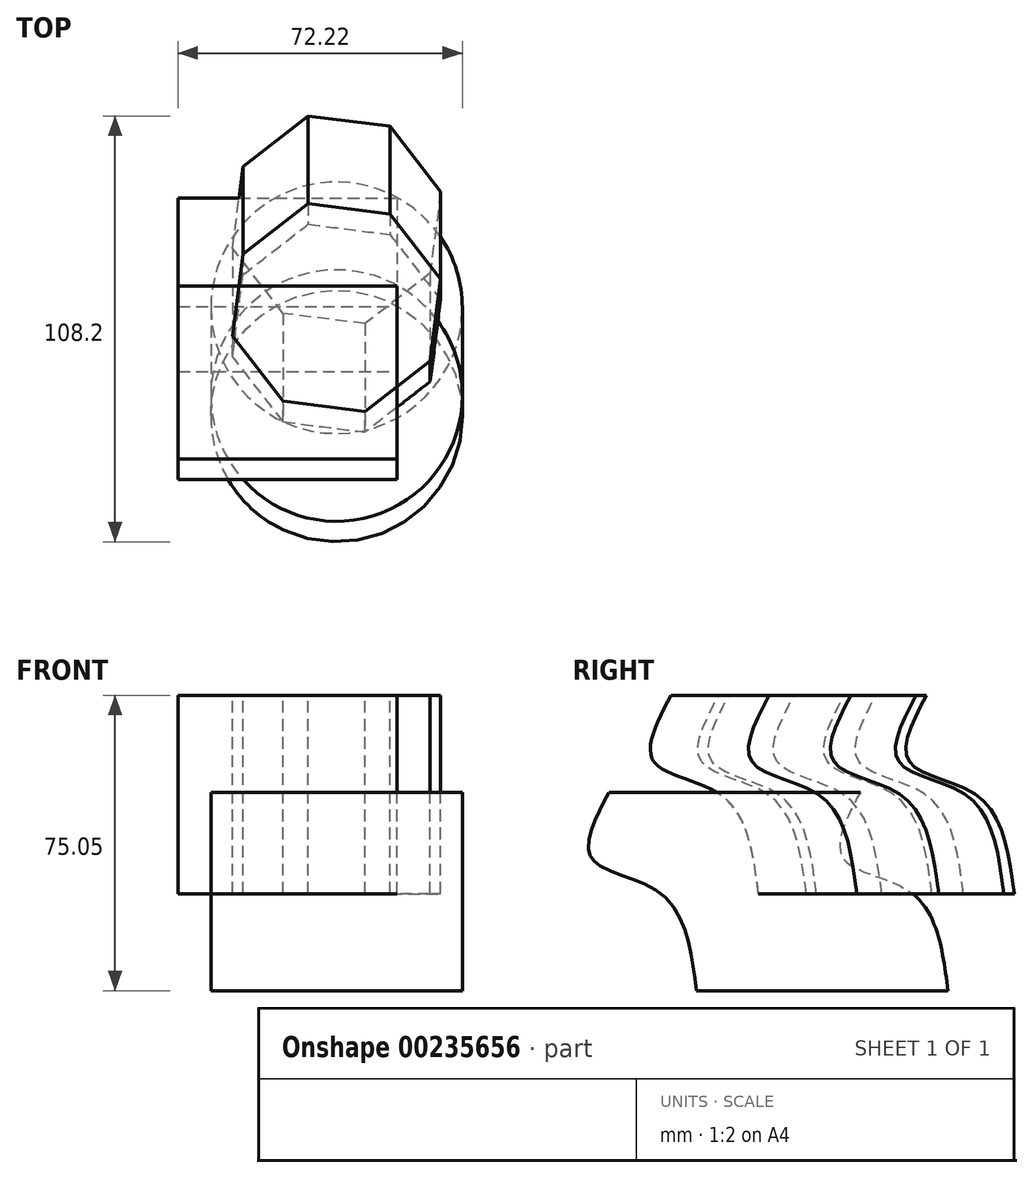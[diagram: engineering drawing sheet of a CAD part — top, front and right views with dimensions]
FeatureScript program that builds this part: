
annotation { "Feature Type Name" : "Feature", "Feature Type Description" : "" }
export const myFeature = defineFeature(function(context is Context, id is Id, definition is map)
    precondition{}
    {
        {
            var Q0;
            Q0=qCreatedBy(makeId("Top.planeOp"),FACE);
            var sketch = newSketch(context, id + "F0", { "sketchPlane" : qUnion([Q0])});
            skCircle(sketch, "E0", {"center": v(0, 0) * mm, "radius": 31.94 * mm});
            skSolve(sketch);
        }
        {
            var Q0;
            Q0=qCreatedBy(makeId("Top.planeOp"),FACE);
            cPlane(context, id + "F1", {"entities" : qUnion([Q0]), "cplaneType" : CPlaneType.OFFSET, "offset" : 25 * mm, "width" : 150 * mm, "height" : 150 * mm});
        }
        {
            var Q0;
            Q0=qCreatedBy(id+"F1.planeOp",FACE);
            var sketch = newSketch(context, id + "F2", { "sketchPlane" : qUnion([Q0])});
            skLineSegment(sketch, "E1.bottom", {"start": v(-40.28, 27.82) * mm, "end": v(15.36, 27.82) * mm});
            skLineSegment(sketch, "E1.top", {"start": v(-40.28, -16.23) * mm, "end": v(15.36, -16.23) * mm});
            skLineSegment(sketch, "E1.left", {"start": v(-40.28, 27.82) * mm, "end": v(-40.28, -16.23) * mm});
            skLineSegment(sketch, "E1.right", {"start": v(15.36, 27.82) * mm, "end": v(15.36, -16.23) * mm});
            skSolve(sketch);
        }
        {
            var Q0;
            Q0=qCreatedBy(id+"F1.planeOp",FACE);
            cPlane(context, id + "F3", {"entities" : qUnion([Q0]), "cplaneType" : CPlaneType.OFFSET, "offset" : 25 * mm, "width" : 150 * mm, "height" : 150 * mm});
        }
        {
            var Q0;
            Q0=qCreatedBy(id+"F3.planeOp",FACE);
            cPlane(context, id + "F4", {"entities" : qUnion([Q0]), "cplaneType" : CPlaneType.OFFSET, "offset" : 25 * mm, "width" : 150 * mm, "height" : 150 * mm});
        }
        {
            var Q0;
            Q0=qCreatedBy(id+"F4.planeOp",FACE);
            var sketch = newSketch(context, id + "F5", { "sketchPlane" : qUnion([Q0])});
            skCircle(sketch, "E2.cCircle", {"center": v(0, 0) * mm, "radius": 25.3 * mm, "construction": true});
            skLineSegment(sketch, "E2.0", {"start": v(23.78, -13.56) * mm, "end": v(7.23, -26.4) * mm});
            skLineSegment(sketch, "E2.1", {"start": v(7.23, -26.4) * mm, "end": v(-13.56, -23.78) * mm});
            skLineSegment(sketch, "E2.2", {"start": v(-13.56, -23.78) * mm, "end": v(-26.4, -7.23) * mm});
            skLineSegment(sketch, "E2.3", {"start": v(-26.4, -7.23) * mm, "end": v(-23.78, 13.56) * mm});
            skLineSegment(sketch, "E2.4", {"start": v(-23.78, 13.56) * mm, "end": v(-7.23, 26.4) * mm});
            skLineSegment(sketch, "E2.5", {"start": v(-7.23, 26.4) * mm, "end": v(13.56, 23.78) * mm});
            skLineSegment(sketch, "E2.6", {"start": v(13.56, 23.78) * mm, "end": v(26.4, 7.23) * mm});
            skLineSegment(sketch, "E2.7", {"start": v(26.4, 7.23) * mm, "end": v(23.78, -13.56) * mm});
            skPoint(sketch, "E2.0.midPoint", {"position": v(15.5, -19.99) * mm});
            skSolve(sketch);
        }
        {
            var Q0;
            Q0=qCreatedBy(makeId("Right.planeOp"),FACE);
            var sketch = newSketch(context, id + "F6", { "sketchPlane" : qUnion([Q0])});
            skLineSegment(sketch, "E3", {"start": v(0, 0) * mm, "end": v(15.36, 24.63) * mm});
            skFitSpline(sketch, "E4", {"points": [v(15.36, 24.63) * mm, v(6.37, 49.26) * mm, v(-11.3, 58.24) * mm, v(-6.95, 75.05) * mm], "startDerivative": vector(-10.38, 79.04) * mm, "endDerivative": vector(33.86, 64.84) * mm});
            skSolve(sketch);
        }
        {
            var Q0;
            Q0=makeQuery(id+"F5.imprint","IMPRINT",FACE,{"disambiguationData":[TD([[makeQuery(id+"F5.imprint","IMPRINT",EDGE,{"derivedFrom":sQuery(id+"F5.wireOp",EDGE,"E2.0")}),-1.0]])]});
            var Q1;
            Q1=makeQuery(id+"F2.imprint","IMPRINT",FACE,{"disambiguationData":[TD([[makeQuery(id+"F2.imprint","IMPRINT",EDGE,{"derivedFrom":sQuery(id+"F2.wireOp",EDGE,"E1.bottom")}),-1.0]])]});
            var Q2;
            Q2=makeQuery(id+"F0.imprint","IMPRINT",FACE,{"disambiguationData":[TD([[makeQuery(id+"F0.imprint","IMPRINT",EDGE,{"derivedFrom":sQuery(id+"F0.wireOp",EDGE,"E0")}),1.0]])]});
            var Q3;
            Q3=sQuery(id+"F6.wireOp",EDGE,"E4");
            sweep(context, id + "F7", {"profiles" : qUnion([Q0, Q1, Q2]), "path" : qUnion([Q3]), "keepProfileOrientation" : true});
        }
    });
